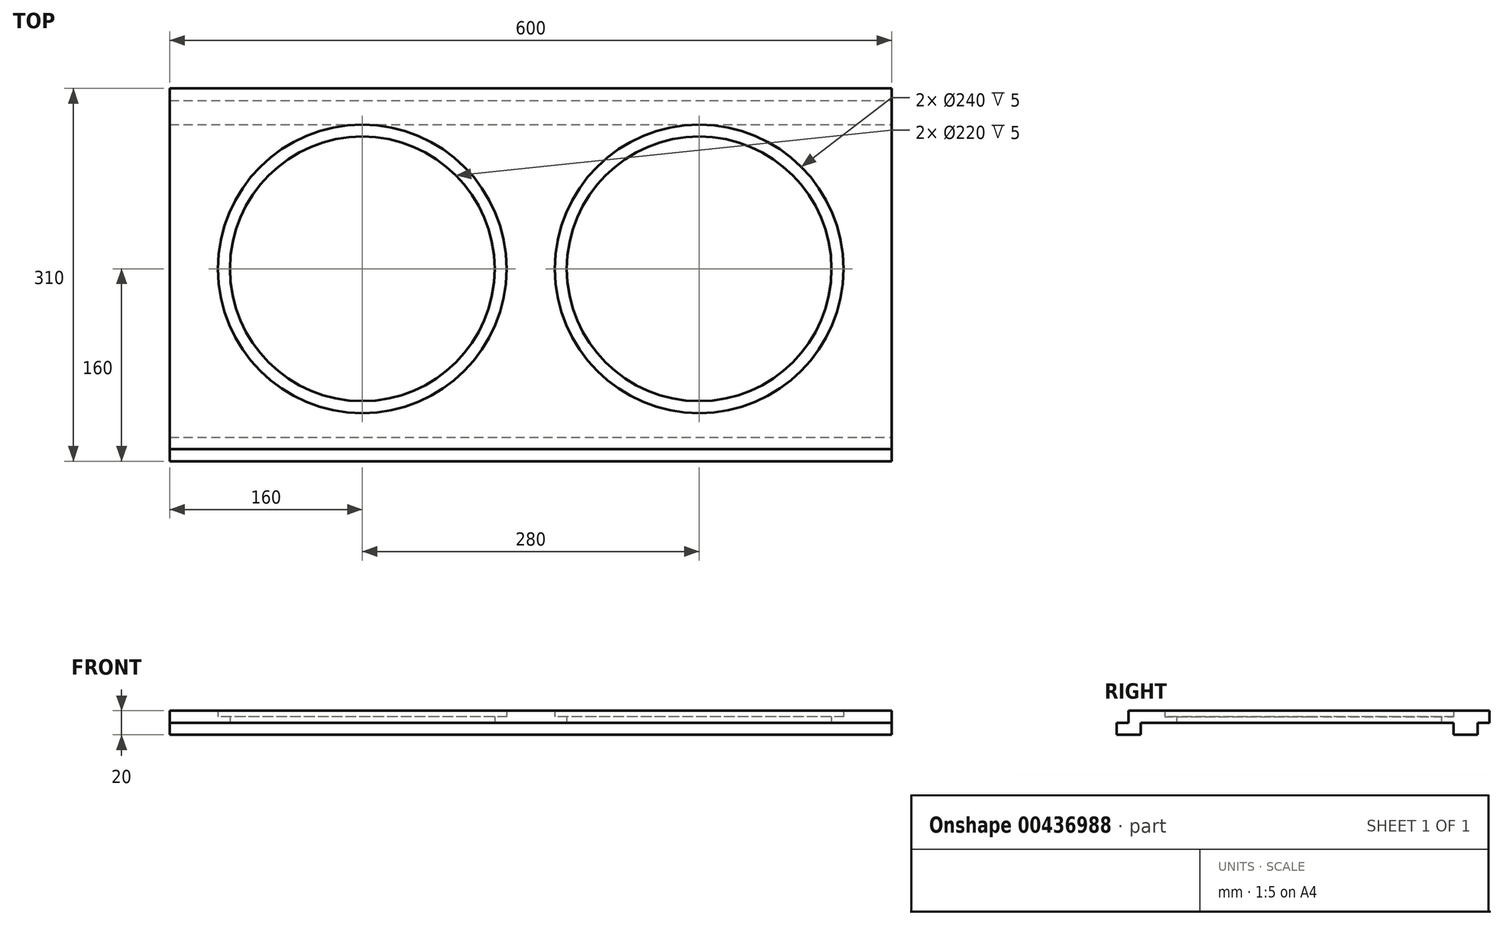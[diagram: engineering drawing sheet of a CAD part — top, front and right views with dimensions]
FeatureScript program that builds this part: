
annotation { "Feature Type Name" : "Feature", "Feature Type Description" : "" }
export const myFeature = defineFeature(function(context is Context, id is Id, definition is map)
    precondition{}
    {
        {
            var Q0;
            Q0=qCreatedBy(makeId("Top.planeOp"),FACE);
            var sketch = newSketch(context, id + "F0", { "sketchPlane" : qUnion([Q0])});
            skLineSegment(sketch, "E0.bottom", {"start": v(300, 150) * mm, "end": v(-300, 150) * mm});
            skLineSegment(sketch, "E0.top", {"start": v(300, -150) * mm, "end": v(-300, -150) * mm});
            skLineSegment(sketch, "E0.left", {"start": v(300, 150) * mm, "end": v(300, -150) * mm});
            skLineSegment(sketch, "E0.right", {"start": v(-300, 150) * mm, "end": v(-300, -150) * mm});
            skPoint(sketch, "E0.middle", {"position": v(0, 0) * mm});
            skLineSegment(sketch, "E1", {"start": v(-300, 0) * mm, "end": v(300, 0) * mm, "construction": true});
            skCircle(sketch, "E2", {"center": v(-140, 0) * mm, "radius": 120 * mm});
            skCircle(sketch, "E3", {"center": v(140, 0) * mm, "radius": 120 * mm});
            skCircle(sketch, "E4", {"center": v(140, 0) * mm, "radius": 110 * mm});
            skCircle(sketch, "E5", {"center": v(-140, 0) * mm, "radius": 110 * mm});
            skSolve(sketch);
        }
        {
            var Q0;
            Q0=makeQuery(id+"F0.imprint","IMPRINT",FACE,{"disambiguationData":[TD([[makeQuery(id+"F0.imprint","IMPRINT",EDGE,{"derivedFrom":sQuery(id+"F0.wireOp",EDGE,"E0.bottom")}),1.0]])]});
            extrude(context, id + "F1", {"entities" : qUnion([Q0]), "depth" : 10 * mm});
        }
        {
            var Q0;
            Q0=makeQuery(id+"F0.imprint","IMPRINT",FACE,{"disambiguationData":[TD([[makeQuery(id+"F0.imprint","IMPRINT",EDGE,{"derivedFrom":sQuery(id+"F0.wireOp",EDGE,"E2")}),1.0]])]});
            var Q1;
            Q1=makeQuery(id+"F0.imprint","IMPRINT",FACE,{"disambiguationData":[TD([[makeQuery(id+"F0.imprint","IMPRINT",EDGE,{"derivedFrom":sQuery(id+"F0.wireOp",EDGE,"E3")}),1.0]])]});
            extrude(context, id + "F2", {"entities" : qUnion([Q0, Q1]), "operationType" : NewBodyOperationType.ADD, "depth" : 5 * mm});
        }
        {
            var Q0;
            Q0=makeQuery(id+"F0.imprint","IMPRINT",FACE,{"disambiguationData":[TD([[makeQuery(id+"F0.imprint","IMPRINT",EDGE,{"derivedFrom":sQuery(id+"F0.wireOp",EDGE,"E0.bottom")}),1.0]])]});
            var sketch = newSketch(context, id + "F3", { "sketchPlane" : qUnion([Q0])});
            skLineSegment(sketch, "E6.0", {"start": v(-300, 150) * mm, "end": v(-300, -150) * mm, "construction": true});
            skLineSegment(sketch, "E7.0", {"start": v(300, 150) * mm, "end": v(300, -150) * mm, "construction": true});
            skLineSegment(sketch, "E8.0", {"start": v(300, -150) * mm, "end": v(-300, -150) * mm, "construction": true});
            skLineSegment(sketch, "E9.0", {"start": v(300, 150) * mm, "end": v(-300, 150) * mm, "construction": true});
            skLineSegment(sketch, "E10.bottom", {"start": v(-300, 140) * mm, "end": v(300, 140) * mm});
            skLineSegment(sketch, "E10.top", {"start": v(-300, 120) * mm, "end": v(300, 120) * mm});
            skLineSegment(sketch, "E10.left", {"start": v(-300, 140) * mm, "end": v(-300, 120) * mm});
            skLineSegment(sketch, "E10.right", {"start": v(300, 140) * mm, "end": v(300, 120) * mm});
            skLineSegment(sketch, "E11.bottom", {"start": v(-300, -140) * mm, "end": v(300, -140) * mm});
            skLineSegment(sketch, "E11.top", {"start": v(-300, -160) * mm, "end": v(300, -160) * mm});
            skLineSegment(sketch, "E11.left", {"start": v(-300, -140) * mm, "end": v(-300, -160) * mm});
            skLineSegment(sketch, "E11.right", {"start": v(300, -140) * mm, "end": v(300, -160) * mm});
            skSolve(sketch);
        }
        {
            var Q0;
            {var subQ0=sQuery(id+"F3.wireOp",EDGE,"E11.bottom");Q0=makeQuery(id+"F3.imprint","IMPRINT",FACE,{"disambiguationData":[TD([[makeQuery(id+"F3.imprint","IMPRINT",EDGE,{"derivedFrom":subQ0}),-1.0]])]});}
            var Q1;
            {var subQ0=sQuery(id+"F3.wireOp",EDGE,"E11.top");Q1=makeQuery(id+"F3.imprint","IMPRINT",FACE,{"disambiguationData":[TD([[makeQuery(id+"F3.imprint","IMPRINT",EDGE,{"derivedFrom":subQ0}),1.0]])]});}
            var Q2;
            Q2=makeQuery(id+"F3.imprint","IMPRINT",FACE,{"disambiguationData":[TD([[makeQuery(id+"F3.imprint","IMPRINT",EDGE,{"derivedFrom":sQuery(id+"F3.wireOp",EDGE,"E10.bottom")}),-1.0]])]});
            extrude(context, id + "F4", {"entities" : qUnion([Q0, Q1, Q2]), "operationType" : NewBodyOperationType.ADD, "oppositeDirection" : true, "depth" : 10 * mm});
        }
    });
